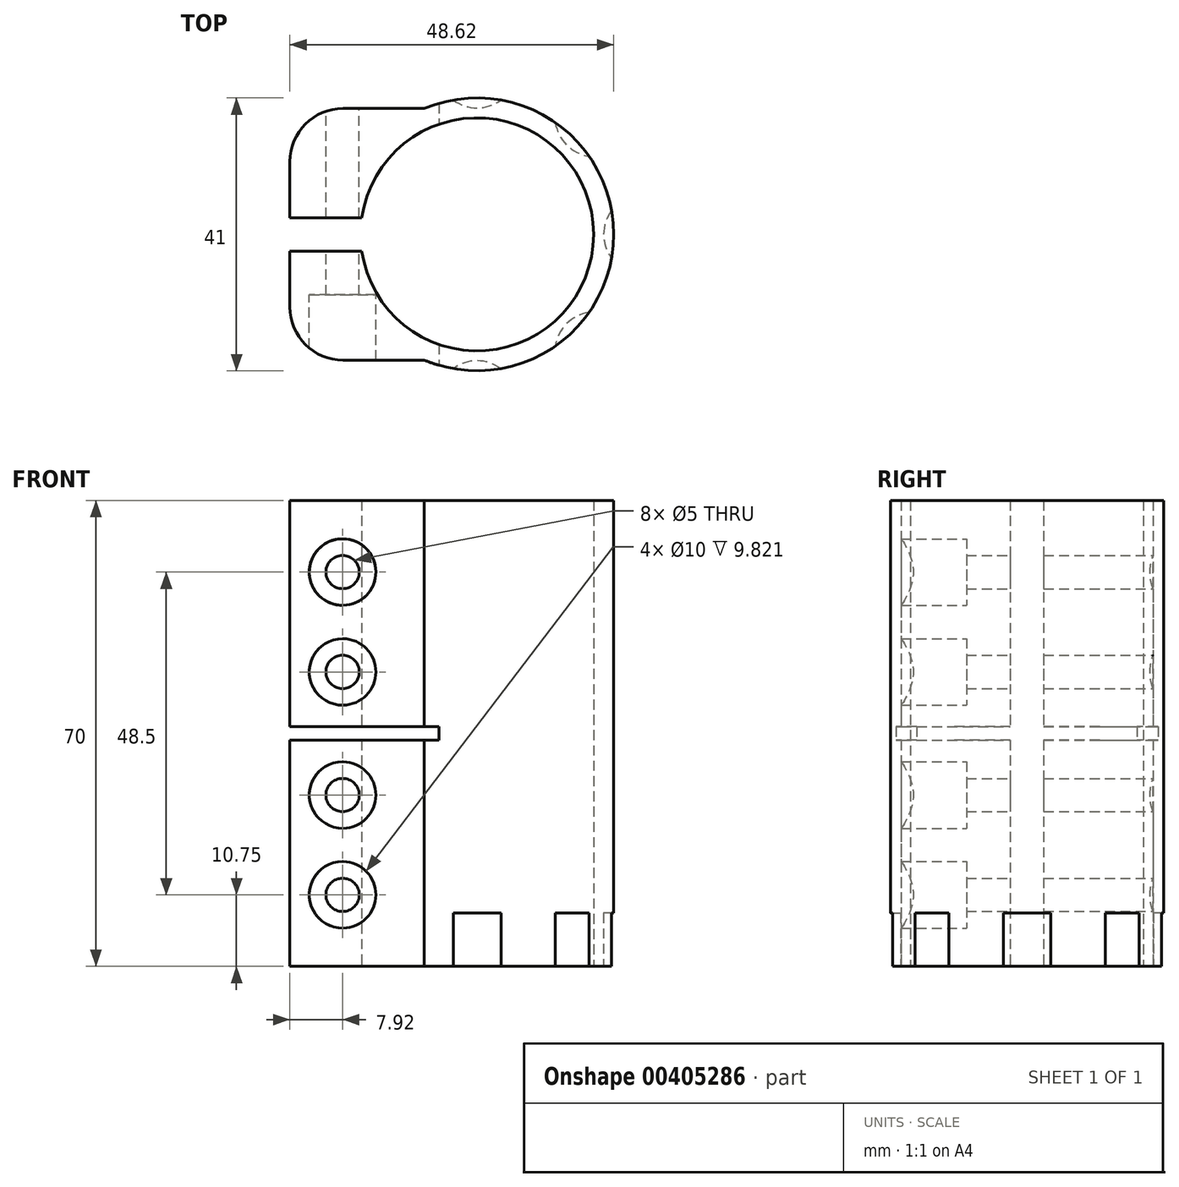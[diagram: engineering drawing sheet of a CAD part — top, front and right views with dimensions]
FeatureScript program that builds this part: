
annotation { "Feature Type Name" : "Feature", "Feature Type Description" : "" }
export const myFeature = defineFeature(function(context is Context, id is Id, definition is map)
    precondition{}
    {
        {
            var Q0;
            Q0=qCreatedBy(makeId("Top.planeOp"),FACE);
            var sketch = newSketch(context, id + "F0", { "sketchPlane" : qUnion([Q0])});
            skArc(sketch, "E0", {"start": v(-17.32, -2.5) * mm, "mid": v(17.5, 0) * mm, "end": v(-17.32, 2.5) * mm});
            skLineSegment(sketch, "E1", {"start": v(-7.92, 18.9) * mm, "end": v(-20.12, 18.9) * mm});
            skLineSegment(sketch, "E2", {"start": v(-28.12, 10.9) * mm, "end": v(-28.12, 2.5) * mm});
            skLineSegment(sketch, "E3", {"start": v(-28.12, 2.5) * mm, "end": v(-17.32, 2.5) * mm});
            skPoint(sketch, "E4.visualSharp", {"position": v(-28.12, 18.9) * mm});
            skArc(sketch, "E4.filletArc", {"start": v(-20.12, 18.9) * mm, "mid": v(-25.78, 16.57) * mm, "end": v(-28.12, 10.9) * mm});
            skLineSegment(sketch, "E5.MirrorCS", {"start": v(-7.92, -18.9) * mm, "end": v(-20.12, -18.9) * mm});
            skArc(sketch, "E6.MirrorCS", {"start": v(-20.12, -18.9) * mm, "mid": v(-25.78, -16.57) * mm, "end": v(-28.12, -10.9) * mm});
            skLineSegment(sketch, "E7.MirrorCS", {"start": v(-28.12, -2.5) * mm, "end": v(-17.32, -2.5) * mm});
            skLineSegment(sketch, "E8.MirrorCS", {"start": v(-28.12, -10.9) * mm, "end": v(-28.12, -2.5) * mm});
            skArc(sketch, "E9.trimOffspring", {"start": v(-7.92, -18.9) * mm, "mid": v(20.5, 0) * mm, "end": v(-7.92, 18.9) * mm});
            skSolve(sketch);
        }
        {
            var Q0;
            Q0 = qSketchRegion(id + "F0", true);
            extrude(context, id + "F1", {"entities" : qUnion([Q0]), "depth" : 70 * mm, "symmetric" : true});
        }
        {
            var Q0;
            Q0=makeQuery(id+"F1.opExtrude","SWEPT_FACE",FACE,{"disambiguationData":[OSD([sQuery(id+"F0.wireOp",EDGE,"E5.MirrorCS")])]});
            var sketch = newSketch(context, id + "F2", { "sketchPlane" : qUnion([Q0])});
            skPoint(sketch, "E10", {"position": v(-20.2, -24.25) * mm});
            skPoint(sketch, "E11", {"position": v(-20.2, -9.25) * mm});
            skPoint(sketch, "E12", {"position": v(-20.2, 9.25) * mm});
            skPoint(sketch, "E13", {"position": v(-20.2, 24.25) * mm});
            skSolve(sketch);
        }
        {
            var Q0;
            Q0=sQuery(id+"F2.wireOp",VERTEX,"E10");
            var Q1;
            Q1=sQuery(id+"F2.wireOp",VERTEX,"E11");
            var Q2;
            Q2=sQuery(id+"F2.wireOp",VERTEX,"E12");
            var Q3;
            Q3=sQuery(id+"F2.wireOp",VERTEX,"E13");
            var Q4;
            Q4=makeQuery(id+"F1.opExtrude","SWEPT_BODY",BODY,{"disambiguationData":[OSD([sQuery(id+"F0.wireOp",EDGE,"E0"),sQuery(id+"F0.wireOp",EDGE,"E1"),sQuery(id+"F0.wireOp",EDGE,"E2"),sQuery(id+"F0.wireOp",EDGE,"E3"),sQuery(id+"F0.wireOp",EDGE,"E4.filletArc"),sQuery(id+"F0.wireOp",EDGE,"E5.MirrorCS"),sQuery(id+"F0.wireOp",EDGE,"E6.MirrorCS"),sQuery(id+"F0.wireOp",EDGE,"E7.MirrorCS"),sQuery(id+"F0.wireOp",EDGE,"E8.MirrorCS"),sQuery(id+"F0.wireOp",EDGE,"E9.trimOffspring")])]});
            hole(context, id + "F3", {"style" : HoleStyle.C_BORE, "endStyle" : HoleEndStyle.THROUGH, "holeDiameter" : 5 * mm, "cBoreDiameter" : 10 * mm, "cBoreDepth" : 8 * mm, "isTappedThrough" : true, "tappedDepth" : 12 * mm, "tapClearance" : 3, "locations" : qUnion([Q0, Q1, Q2, Q3]), "scope" : qUnion([Q4])});
        }
        {
            var Q0;
            Q0=qCreatedBy(makeId("Front.planeOp"),FACE);
            var sketch = newSketch(context, id + "F4", { "sketchPlane" : qUnion([Q0])});
            skLineSegment(sketch, "E14.bottom", {"start": v(-28.12, 1) * mm, "end": v(-5.72, 1) * mm});
            skLineSegment(sketch, "E14.top", {"start": v(-28.12, -1) * mm, "end": v(-5.72, -1) * mm});
            skLineSegment(sketch, "E14.left", {"start": v(-28.12, 1) * mm, "end": v(-28.12, -1) * mm});
            skLineSegment(sketch, "E14.right", {"start": v(-5.72, 1) * mm, "end": v(-5.72, -1) * mm});
            skSolve(sketch);
        }
        {
            var Q0;
            Q0 = qSketchRegion(id + "F4", true);
            extrude(context, id + "F5", {"entities" : qUnion([Q0]), "operationType" : NewBodyOperationType.REMOVE, "oppositeDirection" : true, "depth" : 50 * mm, "symmetric" : true});
        }
        {
            var Q0;
            Q0=makeQuery(id+"F1.opExtrude","CAP_FACE",FACE,{"disambiguationData":[OSD([sQuery(id+"F0.wireOp",EDGE,"E0"),sQuery(id+"F0.wireOp",EDGE,"E1"),sQuery(id+"F0.wireOp",EDGE,"E2"),sQuery(id+"F0.wireOp",EDGE,"E3"),sQuery(id+"F0.wireOp",EDGE,"E4.filletArc"),sQuery(id+"F0.wireOp",EDGE,"E5.MirrorCS"),sQuery(id+"F0.wireOp",EDGE,"E6.MirrorCS"),sQuery(id+"F0.wireOp",EDGE,"E7.MirrorCS"),sQuery(id+"F0.wireOp",EDGE,"E8.MirrorCS"),sQuery(id+"F0.wireOp",EDGE,"E9.trimOffspring")])],"isStart":true});
            var sketch = newSketch(context, id + "F6", { "sketchPlane" : qUnion([Q0])});
            skCircle(sketch, "E15", {"center": v(0, 25) * mm, "radius": 6 * mm});
            skCircle(sketch, "E16.1.0", {"center": v(17.68, 17.68) * mm, "radius": 6 * mm});
            skCircle(sketch, "E16.2.0", {"center": v(25, 0) * mm, "radius": 6 * mm});
            skCircle(sketch, "E16.3.0", {"center": v(17.68, -17.68) * mm, "radius": 6 * mm});
            skCircle(sketch, "E16.4.0", {"center": v(0, -25) * mm, "radius": 6 * mm});
            skPoint(sketch, "E16.center", {"position": v(0, 0) * mm});
            skLineSegment(sketch, "E16.anchor1", {"start": v(0, 0) * mm, "end": v(0, 25) * mm, "construction": true});
            skLineSegment(sketch, "E16.anchor2", {"start": v(0, 0) * mm, "end": v(0, -25) * mm, "construction": true});
            skSolve(sketch);
        }
        {
            var Q0;
            Q0 = qSketchRegion(id + "F6", true);
            extrude(context, id + "F7", {"entities" : qUnion([Q0]), "operationType" : NewBodyOperationType.REMOVE, "oppositeDirection" : true, "depth" : 8 * mm});
        }
    });
